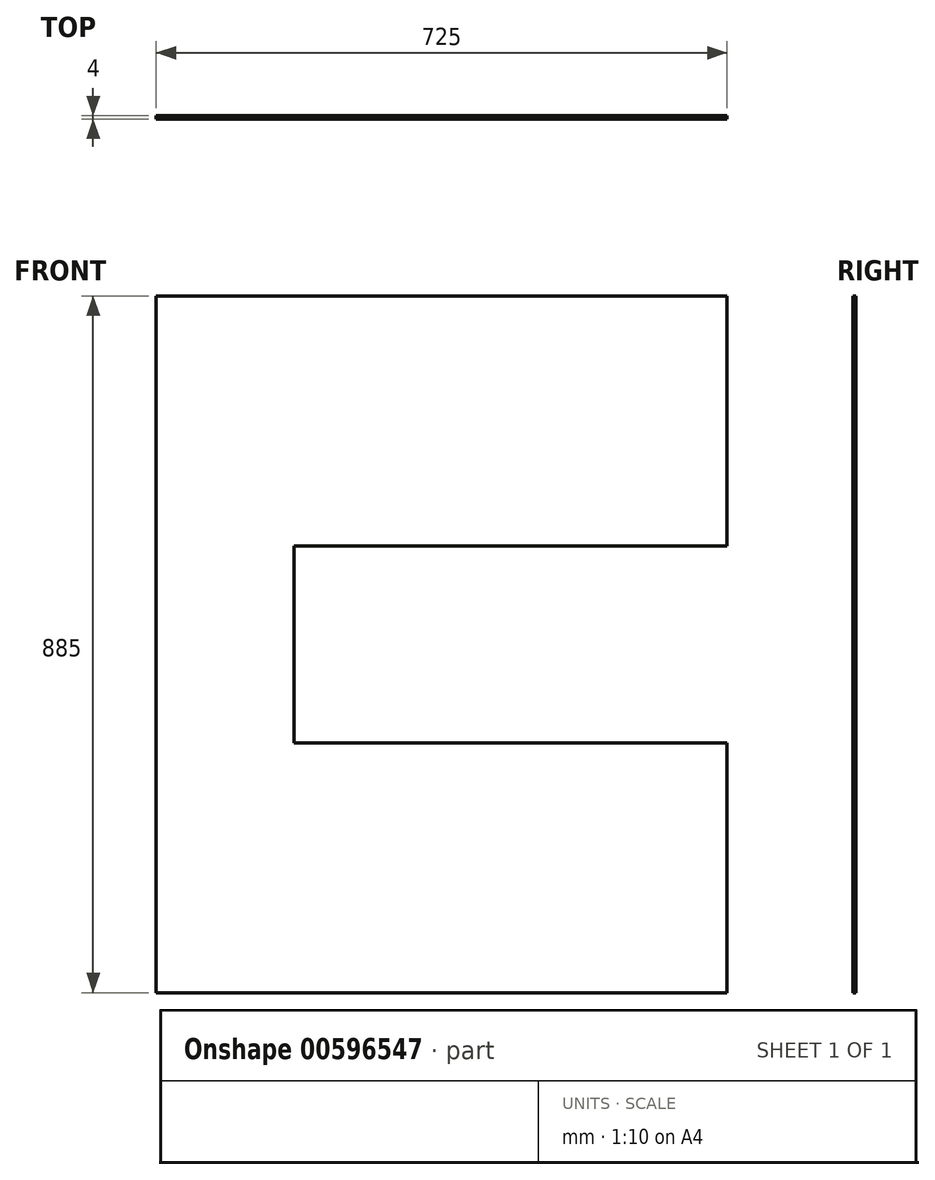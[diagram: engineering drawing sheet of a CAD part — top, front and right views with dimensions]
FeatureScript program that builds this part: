
annotation { "Feature Type Name" : "Feature", "Feature Type Description" : "" }
export const myFeature = defineFeature(function(context is Context, id is Id, definition is map)
    precondition{}
    {
        {
            var Q0;
            Q0=qCreatedBy(makeId("Front.planeOp"),FACE);
            var sketch = newSketch(context, id + "F0", { "sketchPlane" : qUnion([Q0])});
            skLineSegment(sketch, "E0.bottom", {"start": v(0, 0) * mm, "end": v(725, 0) * mm});
            skLineSegment(sketch, "E0.top", {"start": v(0, 885) * mm, "end": v(725, 885) * mm});
            skLineSegment(sketch, "E0.left", {"start": v(0, 0) * mm, "end": v(0, 885) * mm});
            skLineSegment(sketch, "E0.right", {"start": v(725, 0) * mm, "end": v(725, 317.5) * mm});
            skLineSegment(sketch, "E1", {"start": v(175, 442.5) * mm, "end": v(175, 567.5) * mm});
            skLineSegment(sketch, "E2", {"start": v(175, 567.5) * mm, "end": v(725, 567.5) * mm});
            skLineSegment(sketch, "E3.MirrorCS", {"start": v(175, 317.5) * mm, "end": v(725, 317.5) * mm});
            skLineSegment(sketch, "E4", {"start": v(175, 442.5) * mm, "end": v(175, 317.5) * mm});
            skLineSegment(sketch, "E5.trimOffspring", {"start": v(725, 567.5) * mm, "end": v(725, 885) * mm});
            skSolve(sketch);
        }
        {
            var Q0;
            Q0 = qSketchRegion(id + "F0", true);
            extrude(context, id + "F1", {"entities" : qUnion([Q0]), "depth" : 4 * mm, "offsetDistance" : 25 * mm});
        }
    });
